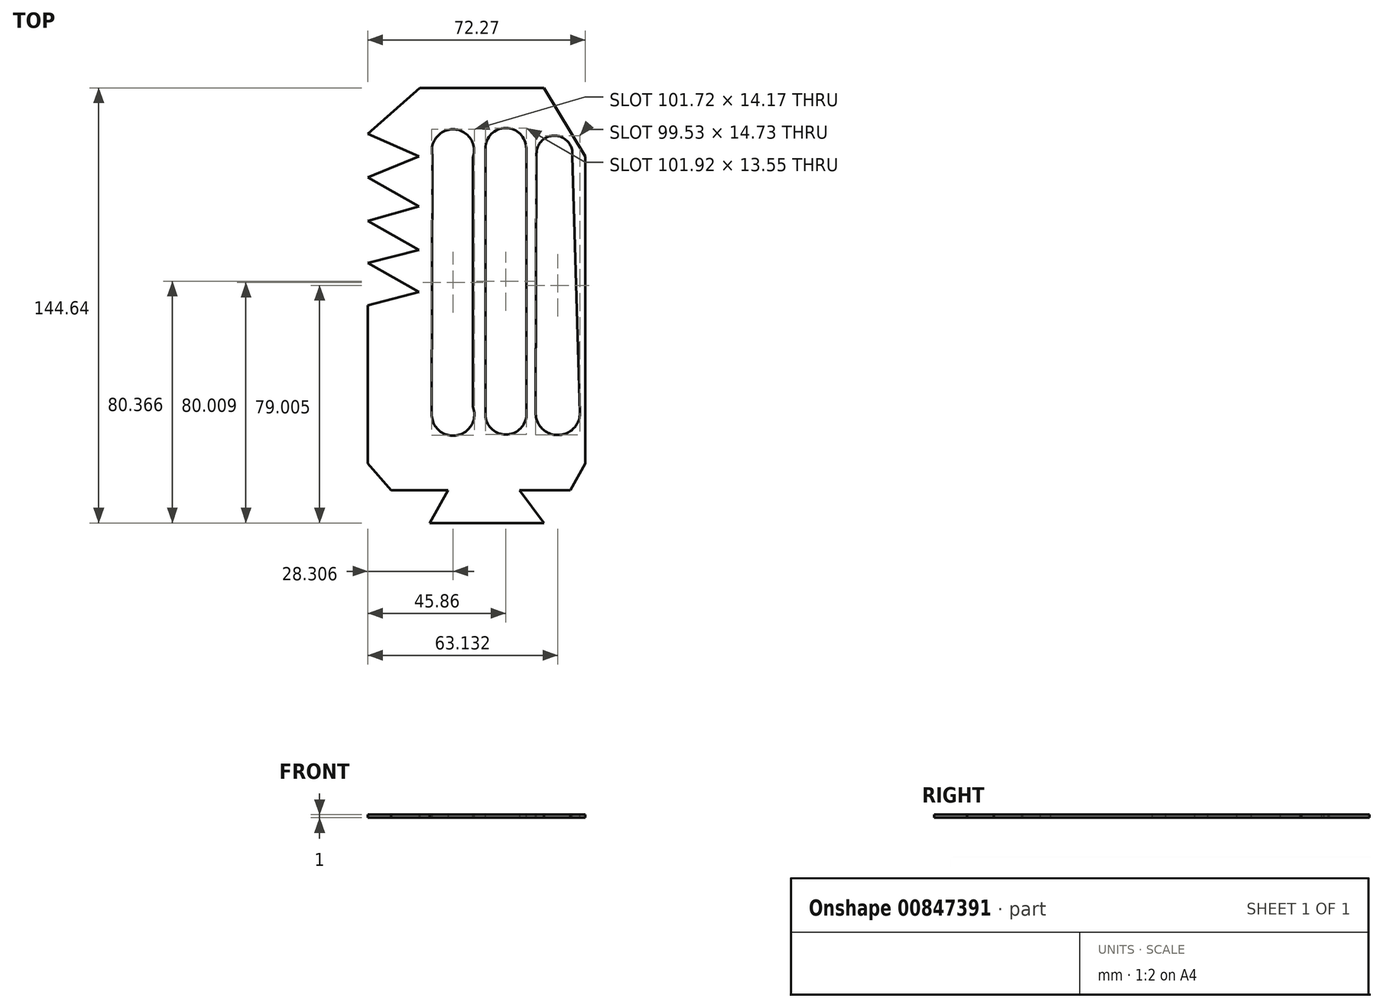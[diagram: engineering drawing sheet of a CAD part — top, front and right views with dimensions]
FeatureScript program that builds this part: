
annotation { "Feature Type Name" : "Feature", "Feature Type Description" : "" }
export const myFeature = defineFeature(function(context is Context, id is Id, definition is map)
    precondition{}
    {
        {
            var Q0;
            Q0=qCreatedBy(makeId("Top.planeOp"),FACE);
            var sketch = newSketch(context, id + "F0", { "sketchPlane" : qUnion([Q0])});
            skLineSegment(sketch, "E0.bottom", {"start": v(-28.61, 85.82) * mm, "end": v(12.65, 85.82) * mm});
            skLineSegment(sketch, "E0.top", {"start": v(-25.35, -58.82) * mm, "end": v(12.65, -58.82) * mm});
            skLineSegment(sketch, "E1", {"start": v(-28.61, 85.82) * mm, "end": v(-45.86, 70.6) * mm});
            skLineSegment(sketch, "E2", {"start": v(-45.86, 70.6) * mm, "end": v(-28.85, 63.1) * mm});
            skLineSegment(sketch, "E3", {"start": v(-28.85, 63.1) * mm, "end": v(-45.86, 56.12) * mm});
            skLineSegment(sketch, "E4", {"start": v(-45.86, 56.12) * mm, "end": v(-28.85, 46.47) * mm});
            skLineSegment(sketch, "E5", {"start": v(-28.85, 46.47) * mm, "end": v(-45.86, 41.64) * mm});
            skLineSegment(sketch, "E6", {"start": v(-45.86, 41.64) * mm, "end": v(-28.85, 31.99) * mm});
            skLineSegment(sketch, "E7", {"start": v(-28.85, 31.99) * mm, "end": v(-45.86, 27.6) * mm});
            skLineSegment(sketch, "E8", {"start": v(-45.86, 27.6) * mm, "end": v(-28.85, 17.95) * mm});
            skLineSegment(sketch, "E9", {"start": v(-28.85, 17.95) * mm, "end": v(-45.86, 13.5) * mm});
            skLineSegment(sketch, "E10", {"start": v(-45.86, 13.5) * mm, "end": v(-45.86, -39.1) * mm});
            skLineSegment(sketch, "E11", {"start": v(-45.86, -39.1) * mm, "end": v(-38.06, -47.88) * mm});
            skLineSegment(sketch, "E12", {"start": v(-38.06, -47.88) * mm, "end": v(-19.14, -47.88) * mm});
            skLineSegment(sketch, "E13", {"start": v(-19.14, -47.88) * mm, "end": v(-25.35, -58.82) * mm});
            skLineSegment(sketch, "E14", {"start": v(12.65, -58.82) * mm, "end": v(4.5, -47.88) * mm});
            skLineSegment(sketch, "E15", {"start": v(4.5, -47.88) * mm, "end": v(21.43, -47.88) * mm});
            skLineSegment(sketch, "E16", {"start": v(21.43, -47.88) * mm, "end": v(26.4, -39.1) * mm});
            skLineSegment(sketch, "E17", {"start": v(26.4, -39.1) * mm, "end": v(26.4, 63.1) * mm});
            skLineSegment(sketch, "E18", {"start": v(26.4, 63.1) * mm, "end": v(12.65, 85.82) * mm});
            skPoint(sketch, "E19.orphan", {"position": v(-45.86, -58.82) * mm});
            skPoint(sketch, "E20.orphan", {"position": v(-45.86, 85.82) * mm});
            skPoint(sketch, "E21.center.orphan", {"position": v(0, -17.97) * mm});
            skSolve(sketch);
        }
        {
            var Q0;
            Q0 = qSketchRegion(id + "F0", true);
            extrude(context, id + "F1", {"entities" : qUnion([Q0]), "depth" : 1 * mm, "offsetDistance" : 25 * mm});
        }
        {
            var Q0;
            Q0=makeQuery(id+"F1.opExtrude","CAP_FACE",FACE,{"disambiguationData":[OSD([sQuery(id+"F0.wireOp",EDGE,"E0.bottom"),sQuery(id+"F0.wireOp",EDGE,"E1"),sQuery(id+"F0.wireOp",EDGE,"E2"),sQuery(id+"F0.wireOp",EDGE,"E3"),sQuery(id+"F0.wireOp",EDGE,"E4"),sQuery(id+"F0.wireOp",EDGE,"E5"),sQuery(id+"F0.wireOp",EDGE,"E6"),sQuery(id+"F0.wireOp",EDGE,"E7"),sQuery(id+"F0.wireOp",EDGE,"E8"),sQuery(id+"F0.wireOp",EDGE,"E9"),sQuery(id+"F0.wireOp",EDGE,"E11"),sQuery(id+"F0.wireOp",EDGE,"E12"),sQuery(id+"F0.wireOp",EDGE,"E13"),sQuery(id+"F0.wireOp",EDGE,"E0.top"),sQuery(id+"F0.wireOp",EDGE,"E14"),sQuery(id+"F0.wireOp",EDGE,"E15"),sQuery(id+"F0.wireOp",EDGE,"E16"),sQuery(id+"F0.wireOp",EDGE,"E17"),sQuery(id+"F0.wireOp",EDGE,"E18"),sQuery(id+"F0.wireOp",EDGE,"E10")])],"isStart":false});
            var sketch = newSketch(context, id + "F2", { "sketchPlane" : qUnion([Q0])});
            skArc(sketch, "E22", {"start": v(-10.94, 62.63) * mm, "mid": v(-17.1, 72.05) * mm, "end": v(-24.4, 63.48) * mm});
            skArc(sketch, "E23", {"start": v(-24.64, -22.68) * mm, "mid": v(-16.24, -29.67) * mm, "end": v(-10.94, -20.11) * mm});
            skArc(sketch, "E24", {"start": v(-6.78, -23.6) * mm, "mid": v(0, -29.41) * mm, "end": v(6.78, -23.6) * mm});
            skArc(sketch, "E25", {"start": v(6.78, 65.73) * mm, "mid": v(0, 72.5) * mm, "end": v(-6.78, 65.73) * mm});
            skArc(sketch, "E26", {"start": v(9.9, -22.2) * mm, "mid": v(17.37, -29.58) * mm, "end": v(24.64, -22) * mm});
            skArc(sketch, "E27", {"start": v(22.06, 63.1) * mm, "mid": v(16.6, 69.95) * mm, "end": v(10.18, 64) * mm});
            skLineSegment(sketch, "E28", {"start": v(-24.39, 66.63) * mm, "end": v(-24.64, -22.68) * mm});
            skLineSegment(sketch, "E29", {"start": v(-10.94, 67.44) * mm, "end": v(-10.94, -20.11) * mm});
            skLineSegment(sketch, "E30", {"start": v(-6.78, 65.73) * mm, "end": v(-6.78, -23.6) * mm});
            skLineSegment(sketch, "E31", {"start": v(6.78, 65.73) * mm, "end": v(6.78, -23.6) * mm});
            skLineSegment(sketch, "E32", {"start": v(10.18, 64) * mm, "end": v(9.9, -23.6) * mm});
            skLineSegment(sketch, "E33", {"start": v(22.06, 63.1) * mm, "end": v(24.64, -22.22) * mm});
            skSolve(sketch);
        }
        {
            var Q0;
            Q0 = qSketchRegion(id + "F2", true);
            extrude(context, id + "F3", {"entities" : qUnion([Q0]), "operationType" : NewBodyOperationType.REMOVE, "oppositeDirection" : true, "depth" : 1 * mm, "offsetDistance" : 25 * mm});
        }
    });
